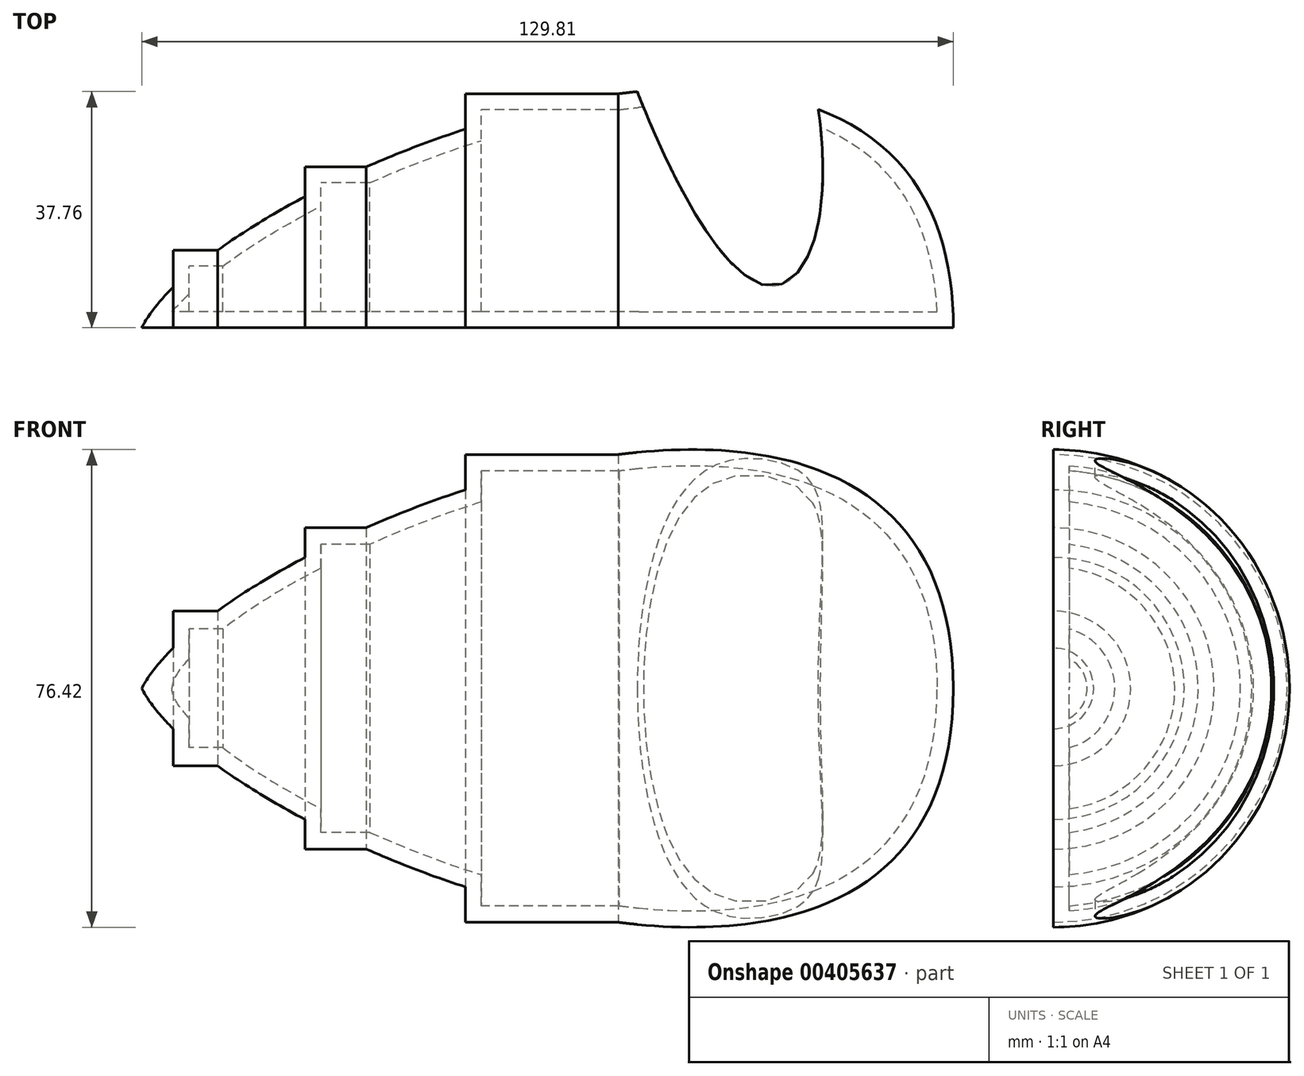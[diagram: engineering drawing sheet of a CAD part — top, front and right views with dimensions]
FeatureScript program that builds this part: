
annotation { "Feature Type Name" : "Feature", "Feature Type Description" : "" }
export const myFeature = defineFeature(function(context is Context, id is Id, definition is map)
    precondition{}
    {
        {
            var Q0;
            Q0=qCreatedBy(makeId("Top.planeOp"),FACE);
            var sketch = newSketch(context, id + "F0", { "sketchPlane" : qUnion([Q0])});
            skLineSegment(sketch, "E0", {"start": v(-76.2, 0) * mm, "end": v(0, 0) * mm});
            skLineSegment(sketch, "E1", {"start": v(0, 0) * mm, "end": v(53.6, 0) * mm});
            skFitSpline(sketch, "E2", {"points": [v(53.6, 0) * mm, v(0, 37.41) * mm, v(-76.2, 0) * mm], "startDerivative": vector(0, 209.53) * mm, "endDerivative": vector(-37.8, -75.42) * mm});
            skLineSegment(sketch, "E3.bottom", {"start": v(0, 0) * mm, "end": v(-24.45, 0) * mm});
            skLineSegment(sketch, "E3.top", {"start": v(0, 37.41) * mm, "end": v(-24.45, 37.41) * mm});
            skLineSegment(sketch, "E3.right", {"start": v(-24.45, 31.76) * mm, "end": v(-24.45, 37.41) * mm});
            skLineSegment(sketch, "E4.bottom", {"start": v(-24.45, 0) * mm, "end": v(-50.1, 0) * mm});
            skLineSegment(sketch, "E4.top", {"start": v(-40.28, 25.71) * mm, "end": v(-50.1, 25.71) * mm});
            skLineSegment(sketch, "E4.right", {"start": v(-50.1, 20.96) * mm, "end": v(-50.1, 25.71) * mm});
            skLineSegment(sketch, "E5.bottom", {"start": v(-50.1, 0) * mm, "end": v(-71.18, 0) * mm});
            skLineSegment(sketch, "E5.top", {"start": v(-64.08, 12.37) * mm, "end": v(-71.18, 12.37) * mm});
            skLineSegment(sketch, "E5.right", {"start": v(-71.18, 6.19) * mm, "end": v(-71.18, 12.37) * mm});
            skPoint(sketch, "E6", {"position": v(-24.45, 31.76) * mm});
            skPoint(sketch, "E7", {"position": v(-50.1, 20.96) * mm});
            skPoint(sketch, "E8", {"position": v(-71.18, 6.19) * mm});
            skFitSpline(sketch, "E9", {"points": [v(3.06, 37.76) * mm, v(24.05, 6.7) * mm, v(32.02, 34.92) * mm], "startDerivative": vector(35.57, -91.14) * mm, "endDerivative": vector(-16.16, 120.06) * mm});
            skSolve(sketch);
        }
        {
            var Q0;
            Q0 = qSketchRegion(id + "F0", true);
            var Q1;
            Q1=sQuery(id+"F0.wireOp",EDGE,"E1");
            revolve(context, id + "F1", {"entities" : qUnion([Q0]), "axis" : qUnion([Q1]), "revolveType" : RevolveType.FULL});
        }
        {
            var Q0;
            {var subQ0=sQuery(id+"F0.wireOp",EDGE,"E9");Q0=makeQuery(id+"F0.imprint","IMPRINT",FACE,{"disambiguationData":[TD([[makeQuery(id+"F0.imprint","IMPRINT",EDGE,{"derivedFrom":subQ0}),1.0]])]});}
            extrude(context, id + "F2", {"entities" : qUnion([Q0]), "operationType" : NewBodyOperationType.REMOVE, "oppositeDirection" : true, "depth" : 127 * mm, "symmetric" : true});
        }
        {
            var Q0;
            Q0=qCreatedBy(makeId("Front.planeOp"),FACE);
            var sketch = newSketch(context, id + "F3", { "sketchPlane" : qUnion([Q0])});
            skLineSegment(sketch, "E10.bottom", {"start": v(72.53, 63.59) * mm, "end": v(-130.66, 63.59) * mm});
            skLineSegment(sketch, "E10.top", {"start": v(72.53, -67.56) * mm, "end": v(-130.66, -67.56) * mm});
            skLineSegment(sketch, "E10.left", {"start": v(72.53, 63.59) * mm, "end": v(72.53, -67.56) * mm});
            skLineSegment(sketch, "E10.right", {"start": v(-130.66, 63.59) * mm, "end": v(-130.66, -67.56) * mm});
            skSolve(sketch);
        }
        {
            var Q0;
            Q0 = qSketchRegion(id + "F3", true);
            extrude(context, id + "F4", {"entities" : qUnion([Q0]), "operationType" : NewBodyOperationType.REMOVE, "depth" : 75.7 * mm});
        }
        {
            var Q0;
            Q0=makeQuery(id+"F2.boolean.opBoolean","COPY",FACE,{"derivedFrom":makeQuery(id+"F2.opExtrude","SWEPT_FACE",FACE,{"disambiguationData":[OSD([sQuery(id+"F0.wireOp",EDGE,"E9")])]})});
            shell(context, id + "F5", {"entities" : qUnion([Q0]), "thickness" : 2.54 * mm});
        }
    });
